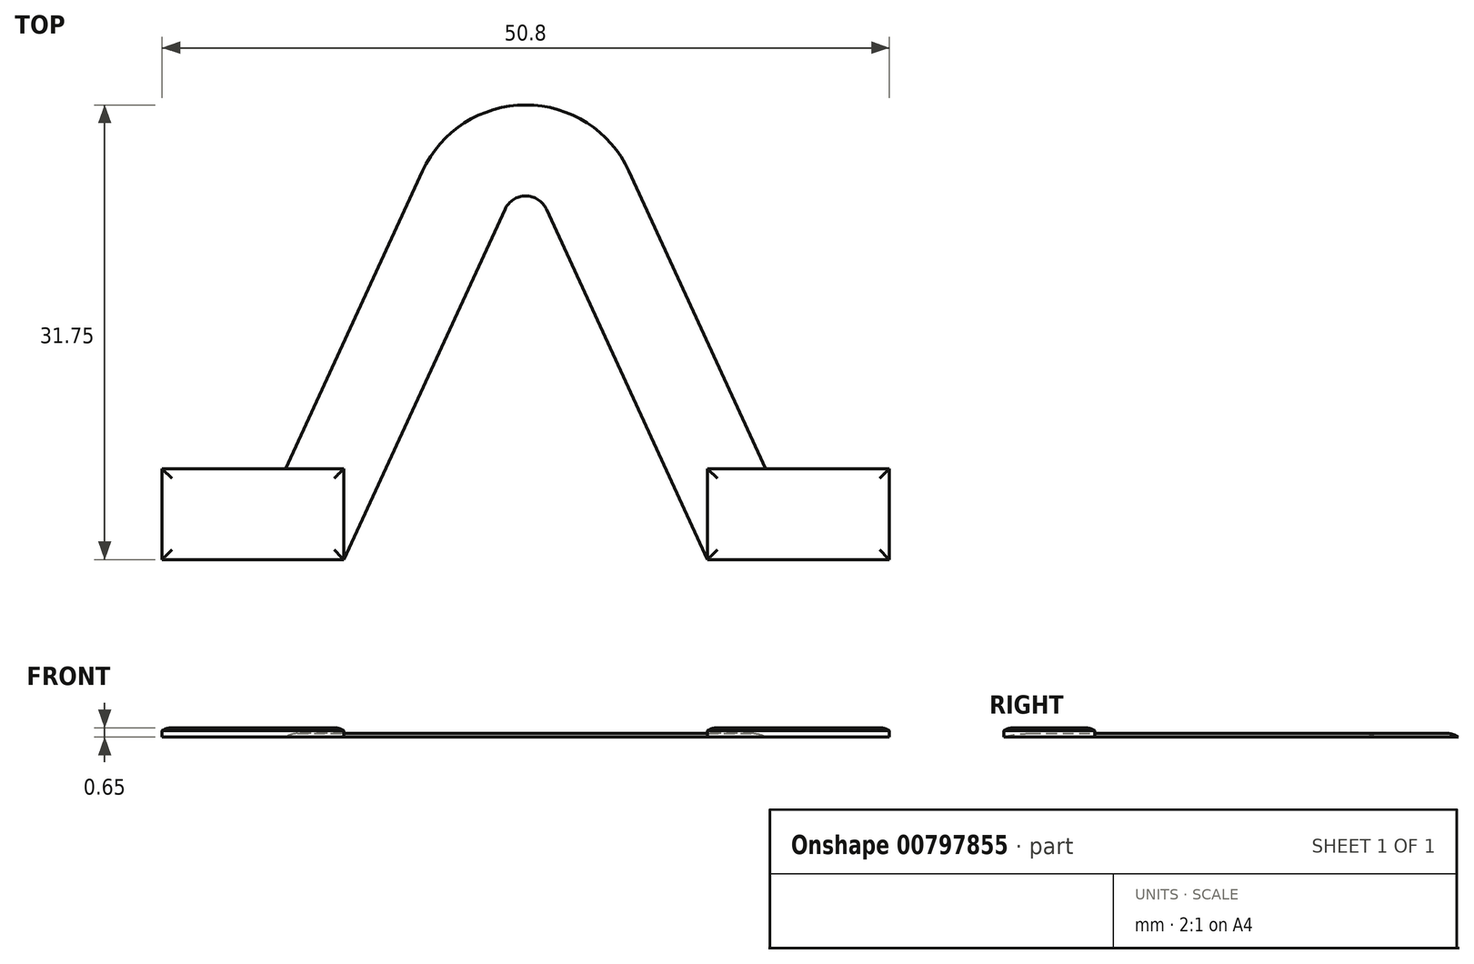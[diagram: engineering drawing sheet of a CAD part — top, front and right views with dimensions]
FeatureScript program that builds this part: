
annotation { "Feature Type Name" : "Feature", "Feature Type Description" : "" }
export const myFeature = defineFeature(function(context is Context, id is Id, definition is map)
    precondition{}
    {
        {
            assignVariable(context, id + "F0", {"name" : "thickness", "anyValue" : 0.25});
        }
        {
            var Q0;
            Q0=qCreatedBy(makeId("Top.planeOp"),FACE);
            var sketch = newSketch(context, id + "F1", { "sketchPlane" : qUnion([Q0])});
            skCircle(sketch, "E0", {"center": v(0, 0) * mm, "radius": 1.59 * mm});
            skLineSegment(sketch, "E1", {"start": v(-1.44, 0.66) * mm, "end": v(-12.7, -23.81) * mm});
            skLineSegment(sketch, "E2", {"start": v(-12.7, -23.81) * mm, "end": v(12.7, -23.81) * mm, "construction": true});
            skLineSegment(sketch, "E3", {"start": v(0, -17.53) * mm, "end": v(0, 5.98) * mm, "construction": true});
            skPoint(sketch, "E4", {"position": v(0, -23.81) * mm});
            skLineSegment(sketch, "E5", {"start": v(12.7, -23.81) * mm, "end": v(1.44, 0.66) * mm});
            skLineSegment(sketch, "E6.bottom", {"start": v(-12.7, -23.81) * mm, "end": v(-25.4, -23.81) * mm});
            skLineSegment(sketch, "E6.top", {"start": v(-12.7, -17.46) * mm, "end": v(-25.4, -17.46) * mm});
            skLineSegment(sketch, "E6.left", {"start": v(-12.7, -23.81) * mm, "end": v(-12.7, -17.46) * mm});
            skLineSegment(sketch, "E6.right", {"start": v(-25.4, -23.81) * mm, "end": v(-25.4, -17.46) * mm});
            skLineSegment(sketch, "E7.bottom", {"start": v(12.7, -23.81) * mm, "end": v(25.4, -23.81) * mm});
            skLineSegment(sketch, "E7.top", {"start": v(12.7, -17.46) * mm, "end": v(25.4, -17.46) * mm});
            skLineSegment(sketch, "E7.left", {"start": v(12.7, -23.81) * mm, "end": v(12.7, -17.46) * mm});
            skLineSegment(sketch, "E7.right", {"start": v(25.4, -23.81) * mm, "end": v(25.4, -17.46) * mm});
            skLineSegment(sketch, "E8", {"start": v(-7.21, 3.32) * mm, "end": v(-16.77, -17.46) * mm});
            skLineSegment(sketch, "E9", {"start": v(7.21, 3.32) * mm, "end": v(16.77, -17.46) * mm});
            skCircle(sketch, "E10", {"center": v(0, 0) * mm, "radius": 7.94 * mm});
            skLineSegment(sketch, "E11", {"start": v(-21.36, 7.94) * mm, "end": v(20.35, 7.94) * mm, "construction": true});
            skSolve(sketch);
        }
        {
            var Q0;
            Q0=makeQuery(id+"F1.imprint","IMPRINT",FACE,{"disambiguationData":[TD([[makeQuery(id+"F1.imprint","IMPRINT",EDGE,{"derivedFrom":sQuery(id+"F1.wireOp",EDGE,"E6.bottom")}),-1.0]])]});
            var Q1;
            {var subQ1=sQuery(id+"F1.wireOp",EDGE,"E6.left");Q1=makeQuery(id+"F1.imprint","IMPRINT",FACE,{"disambiguationData":[TD([[makeQuery(id+"F1.imprint","IMPRINT",EDGE,{"derivedFrom":subQ1}),-1.0]])]});}
            var Q2;
            {var subQ3=sQuery(id+"F1.wireOp",EDGE,"E1");var subQ4=sQuery(id+"F1.wireOp",EDGE,"E0");var subQ5=makeQuery(id+"F1.imprint","INTERSECT",VERTEX,{"derivedFrom":[subQ4,subQ3]});Q2=makeQuery(id+"F1.imprint","IMPRINT",FACE,{"disambiguationData":[TD([[makeQuery(id+"F1.imprint","IMPRINT",EDGE,{"disambiguationData":[TD([[subQ5,1.0]])],"derivedFrom":subQ4}),-1.0]])]});}
            var Q3;
            {var subQ1=sQuery(id+"F1.wireOp",EDGE,"E7.left");Q3=makeQuery(id+"F1.imprint","IMPRINT",FACE,{"disambiguationData":[TD([[makeQuery(id+"F1.imprint","IMPRINT",EDGE,{"derivedFrom":subQ1}),1.0]])]});}
            var Q4;
            Q4=makeQuery(id+"F1.imprint","IMPRINT",FACE,{"disambiguationData":[TD([[makeQuery(id+"F1.imprint","IMPRINT",EDGE,{"derivedFrom":sQuery(id+"F1.wireOp",EDGE,"E7.bottom")}),1.0]])]});
            extrude(context, id + "F2", {"entities" : qUnion([Q0, Q1, Q2, Q3, Q4]), "depth" : (getVariable(context, 'thickness')) * mm, "offsetDistance" : 25.4 * mm});
        }
        {
            assignVariable(context, id + "F3", {"name" : "depth", "anyValue" : .4});
        }
        {
            var Q0;
            Q0=makeQuery(id+"F2.opExtrude","CAP_FACE",FACE,{"disambiguationData":[OSD([sQuery(id+"F1.wireOp",EDGE,"E0"),sQuery(id+"F1.wireOp",EDGE,"E1"),sQuery(id+"F1.wireOp",EDGE,"E5"),sQuery(id+"F1.wireOp",EDGE,"E6.bottom"),sQuery(id+"F1.wireOp",EDGE,"E6.top"),sQuery(id+"F1.wireOp",EDGE,"E6.right"),sQuery(id+"F1.wireOp",EDGE,"E7.bottom"),sQuery(id+"F1.wireOp",EDGE,"E7.top"),sQuery(id+"F1.wireOp",EDGE,"E7.right"),sQuery(id+"F1.wireOp",EDGE,"E8"),sQuery(id+"F1.wireOp",EDGE,"E9"),sQuery(id+"F1.wireOp",EDGE,"E10")])],"isStart":false});
            var sketch = newSketch(context, id + "F4", { "sketchPlane" : qUnion([Q0])});
            skLineSegment(sketch, "E12.0", {"start": v(-12.7, -17.46) * mm, "end": v(-25.4, -17.46) * mm});
            skLineSegment(sketch, "E13.0", {"start": v(-12.7, -23.81) * mm, "end": v(-12.7, -17.46) * mm});
            skLineSegment(sketch, "E14.0", {"start": v(-12.7, -23.81) * mm, "end": v(-25.4, -23.81) * mm});
            skPoint(sketch, "E15.0", {"position": v(-25.4, -20.64) * mm});
            skLineSegment(sketch, "E16.0", {"start": v(-25.4, -23.81) * mm, "end": v(-25.4, -17.46) * mm});
            skLineSegment(sketch, "E17.0", {"start": v(12.7, -17.46) * mm, "end": v(25.4, -17.46) * mm});
            skLineSegment(sketch, "E18.0", {"start": v(12.7, -23.81) * mm, "end": v(12.7, -17.46) * mm});
            skLineSegment(sketch, "E19.0", {"start": v(12.7, -23.81) * mm, "end": v(25.4, -23.81) * mm});
            skLineSegment(sketch, "E20.0", {"start": v(25.4, -23.81) * mm, "end": v(25.4, -17.46) * mm});
            skSolve(sketch);
        }
        {
            var Q0;
            {var subQ0=sQuery(id+"F4.wireOp",EDGE,"E13.0");Q0=makeQuery(id+"F4.imprint","IMPRINT",FACE,{"disambiguationData":[TD([[makeQuery(id+"F4.imprint","IMPRINT",EDGE,{"derivedFrom":subQ0}),1.0]])]});}
            var Q1;
            {var subQ0=sQuery(id+"F4.wireOp",EDGE,"E18.0");Q1=makeQuery(id+"F4.imprint","IMPRINT",FACE,{"disambiguationData":[TD([[makeQuery(id+"F4.imprint","IMPRINT",EDGE,{"derivedFrom":subQ0}),-1.0]])]});}
            extrude(context, id + "F5", {"entities" : qUnion([Q0, Q1]), "operationType" : NewBodyOperationType.ADD, "depth" : (getVariable(context, 'depth') / 2) * mm, "offsetDistance" : 25.4 * mm});
        }
        {
            var Q0;
            Q0=makeQuery(id+"F5.opExtrude","CAP_FACE",FACE,{"disambiguationData":[OSD([sQuery(id+"F4.wireOp",EDGE,"E17.0"),sQuery(id+"F4.wireOp",EDGE,"E18.0"),sQuery(id+"F4.wireOp",EDGE,"E19.0"),sQuery(id+"F4.wireOp",EDGE,"E20.0")])],"isStart":false});
            var Q1;
            Q1=makeQuery(id+"F5.opExtrude","CAP_FACE",FACE,{"disambiguationData":[OSD([sQuery(id+"F4.wireOp",EDGE,"E12.0"),sQuery(id+"F4.wireOp",EDGE,"E13.0"),sQuery(id+"F4.wireOp",EDGE,"E14.0"),sQuery(id+"F4.wireOp",EDGE,"E16.0")])],"isStart":false});
            extrude(context, id + "F6", {"entities" : qUnion([Q0, Q1]), "operationType" : NewBodyOperationType.ADD, "depth" : (getVariable(context, 'depth') / 2) * mm, "offsetDistance" : 25.4 * mm, "hasDraft" : true, "draftAngle" : 10 * degree, "draftPullDirection" : true});
        }
        {
            var Q0;
            Q0=makeQuery(id+"F6.opExtrude","CAP_EDGE",EDGE,{"disambiguationData":[OSD([sQuery(id+"F4.wireOp",EDGE,"E17.0")])],"isStart":false});
            var Q1;
            Q1=makeQuery(id+"F6.opExtrude","CAP_EDGE",EDGE,{"disambiguationData":[OSD([sQuery(id+"F4.wireOp",EDGE,"E18.0")])],"isStart":false});
            var Q2;
            Q2=makeQuery(id+"F6.opExtrude","CAP_EDGE",EDGE,{"disambiguationData":[OSD([sQuery(id+"F4.wireOp",EDGE,"E19.0")])],"isStart":false});
            var Q3;
            Q3=makeQuery(id+"F6.opExtrude","CAP_EDGE",EDGE,{"disambiguationData":[OSD([sQuery(id+"F4.wireOp",EDGE,"E20.0")])],"isStart":false});
            var Q4;
            Q4=makeQuery(id+"F6.opExtrude","CAP_EDGE",EDGE,{"disambiguationData":[OSD([sQuery(id+"F4.wireOp",EDGE,"E12.0")])],"isStart":false});
            var Q5;
            Q5=makeQuery(id+"F6.opExtrude","CAP_EDGE",EDGE,{"disambiguationData":[OSD([sQuery(id+"F4.wireOp",EDGE,"E13.0")])],"isStart":false});
            var Q6;
            Q6=makeQuery(id+"F6.opExtrude","CAP_EDGE",EDGE,{"disambiguationData":[OSD([sQuery(id+"F4.wireOp",EDGE,"E14.0")])],"isStart":false});
            var Q7;
            Q7=makeQuery(id+"F6.opExtrude","CAP_EDGE",EDGE,{"disambiguationData":[OSD([sQuery(id+"F4.wireOp",EDGE,"E16.0")])],"isStart":false});
            var Q8;
            Q8=makeQuery(id+"F2.opExtrude","CAP_EDGE",EDGE,{"disambiguationData":[OSD([sQuery(id+"F1.wireOp",EDGE,"E5")])],"isStart":false});
            var Q9;
            Q9=makeQuery(id+"F2.opExtrude","CAP_EDGE",EDGE,{"disambiguationData":[OSD([sQuery(id+"F1.wireOp",EDGE,"E8")])],"isStart":false});
            fillet(context, id + "F7", {"entities" : qUnion([Q0, Q1, Q2, Q3, Q4, Q5, Q6, Q7, Q8, Q9]), "radius" : 1.27 * mm, "tangentPropagation" : true, "allowEdgeOverflow" : false});
        }
    });
